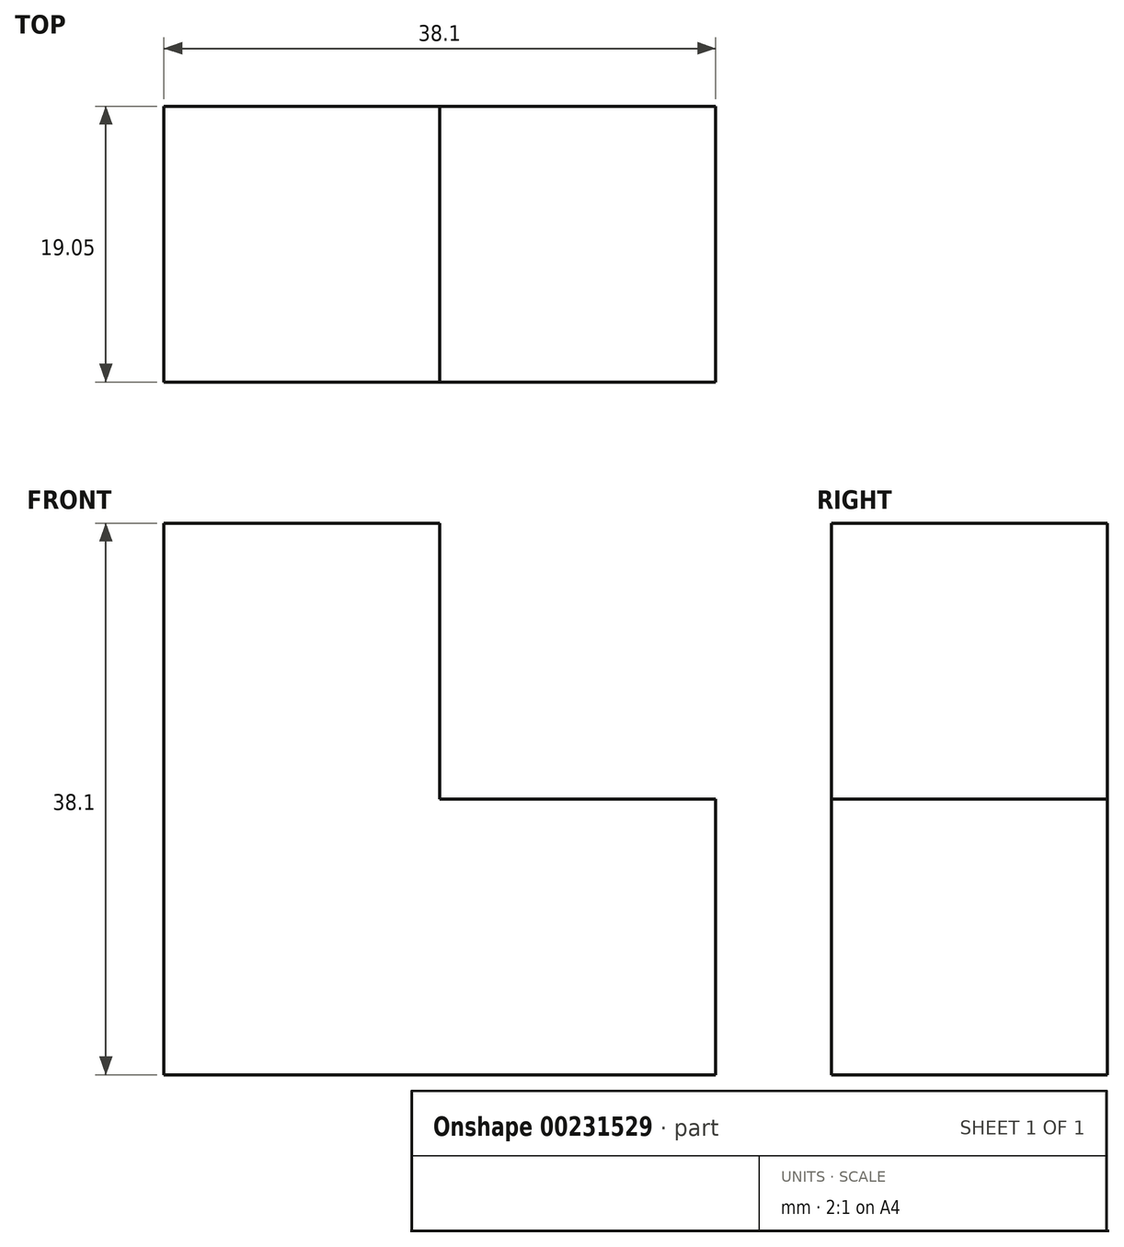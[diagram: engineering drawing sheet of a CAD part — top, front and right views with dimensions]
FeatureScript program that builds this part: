
annotation { "Feature Type Name" : "Feature", "Feature Type Description" : "" }
export const myFeature = defineFeature(function(context is Context, id is Id, definition is map)
    precondition{}
    {
        {
            var Q0;
            Q0=qCreatedBy(makeId("Front.planeOp"),FACE);
            var sketch = newSketch(context, id + "F0", { "sketchPlane" : qUnion([Q0])});
            skLineSegment(sketch, "E0.bottom", {"start": v(-4.63, 14.83) * mm, "end": v(14.42, 14.83) * mm});
            skLineSegment(sketch, "E0.top", {"start": v(-4.63, -23.27) * mm, "end": v(14.42, -23.27) * mm});
            skLineSegment(sketch, "E0.left", {"start": v(-4.63, 14.83) * mm, "end": v(-4.63, -23.27) * mm});
            skLineSegment(sketch, "E0.right", {"start": v(14.42, 14.83) * mm, "end": v(14.42, -23.27) * mm});
            skLineSegment(sketch, "E1.bottom", {"start": v(14.42, -4.22) * mm, "end": v(33.47, -4.22) * mm});
            skLineSegment(sketch, "E1.top", {"start": v(14.42, -23.27) * mm, "end": v(33.47, -23.27) * mm});
            skLineSegment(sketch, "E1.left", {"start": v(14.42, -4.22) * mm, "end": v(14.42, -23.27) * mm});
            skLineSegment(sketch, "E1.right", {"start": v(33.47, -4.22) * mm, "end": v(33.47, -23.27) * mm});
            skSolve(sketch);
        }
        {
            var Q0;
            Q0=makeQuery(id+"F0.imprint","IMPRINT",FACE,{"disambiguationData":[TD([[makeQuery(id+"F0.imprint","IMPRINT",EDGE,{"derivedFrom":sQuery(id+"F0.wireOp",EDGE,"E0.bottom")}),-1.0]])]});
            var Q1;
            Q1=makeQuery(id+"F0.imprint","IMPRINT",FACE,{"disambiguationData":[TD([[makeQuery(id+"F0.imprint","IMPRINT",EDGE,{"derivedFrom":sQuery(id+"F0.wireOp",EDGE,"E1.bottom")}),-1.0]])]});
            extrude(context, id + "F1", {"entities" : qUnion([Q0, Q1]), "depth" : 19.05 * mm});
        }
    });
